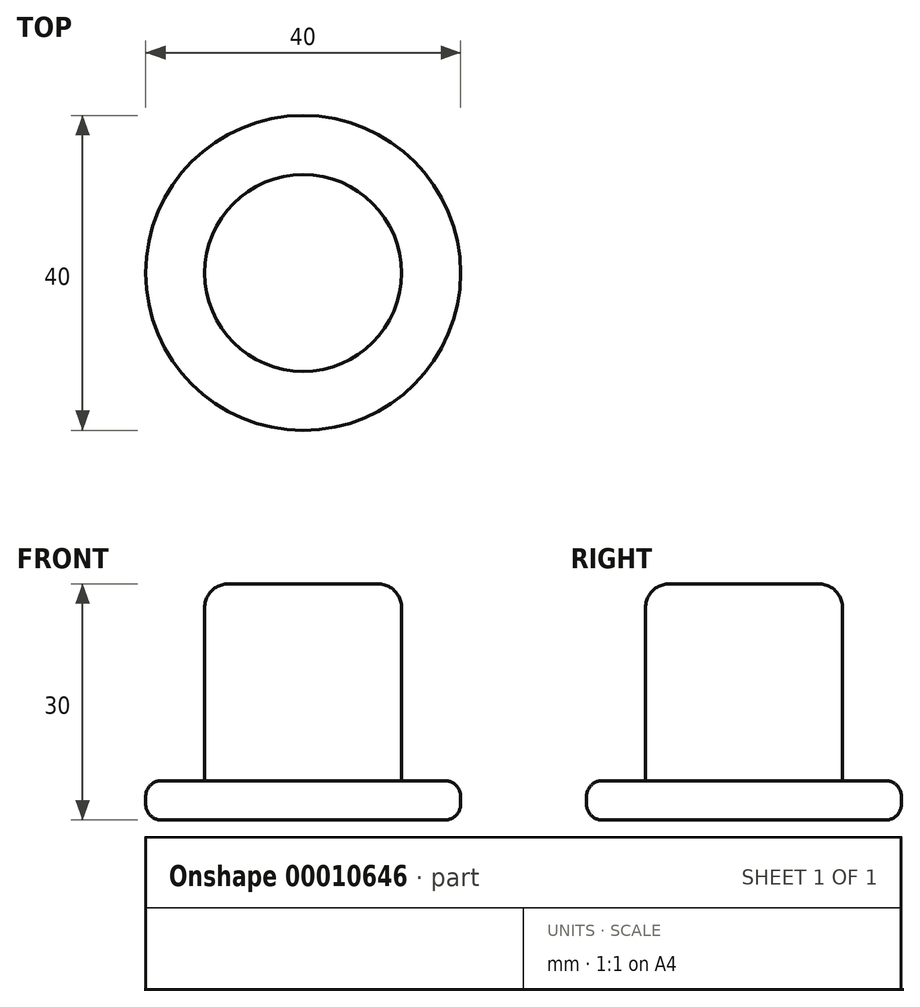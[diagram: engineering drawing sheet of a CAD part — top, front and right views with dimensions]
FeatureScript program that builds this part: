
annotation { "Feature Type Name" : "Feature", "Feature Type Description" : "" }
export const myFeature = defineFeature(function(context is Context, id is Id, definition is map)
    precondition{}
    {
        {
            var Q0;
            Q0=qCreatedBy(makeId("Top.planeOp"),FACE);
            var sketch = newSketch(context, id + "F0", { "sketchPlane" : qUnion([Q0])});
            skCircle(sketch, "E0", {"center": v(0, 0) * mm, "radius": 20 * mm});
            skSolve(sketch);
        }
        {
            var Q0;
            Q0=makeQuery(id+"F0.imprint","IMPRINT",FACE,{"disambiguationData":[TD([[makeQuery(id+"F0.imprint","IMPRINT",EDGE,{"derivedFrom":sQuery(id+"F0.wireOp",EDGE,"E0")}),1.0]])]});
            var Q1;
            Q1=sQuery(id+"F0.wireOp",EDGE,"E0");
            extrude(context, id + "F1", {"entities" : qUnion([Q0]), "surfaceEntities" : qUnion([Q1]), "depth" : 5 * mm});
        }
        {
            var Q0;
            Q0=makeQuery(id+"F1.opExtrude","CAP_EDGE",EDGE,{"disambiguationData":[OSD([sQuery(id+"F0.wireOp",EDGE,"E0")])],"isStart":false});
            var Q1;
            Q1=makeQuery(id+"F1.opExtrude","CAP_EDGE",EDGE,{"disambiguationData":[OSD([sQuery(id+"F0.wireOp",EDGE,"E0")])],"isStart":true});
            fillet(context, id + "F2", {"entities" : qUnion([Q0, Q1]), "radius" : 2 * mm, "tangentPropagation" : true, "allowEdgeOverflow" : false});
        }
        {
            var Q0;
            Q0=makeQuery(id+"F1.opExtrude","CAP_FACE",FACE,{"disambiguationData":[OSD([sQuery(id+"F0.wireOp",EDGE,"E0")])],"isStart":false});
            var sketch = newSketch(context, id + "F3", { "sketchPlane" : qUnion([Q0])});
            skCircle(sketch, "E1", {"center": v(0, 0) * mm, "radius": 12.5 * mm});
            skSolve(sketch);
        }
        {
            var Q0;
            Q0=makeQuery(id+"F3.imprint","IMPRINT",FACE,{"disambiguationData":[TD([[makeQuery(id+"F3.imprint","IMPRINT",EDGE,{"derivedFrom":sQuery(id+"F3.wireOp",EDGE,"E1")}),1.0]])]});
            extrude(context, id + "F4", {"entities" : qUnion([Q0]), "operationType" : NewBodyOperationType.ADD, "depth" : 25 * mm});
        }
        {
            var Q0;
            Q0=makeQuery(id+"F4.opExtrude","CAP_EDGE",EDGE,{"disambiguationData":[OSD([sQuery(id+"F3.wireOp",EDGE,"E1")])],"isStart":false});
            fillet(context, id + "F5", {"entities" : qUnion([Q0]), "radius" : 3 * mm, "tangentPropagation" : true, "allowEdgeOverflow" : false});
        }
    });
